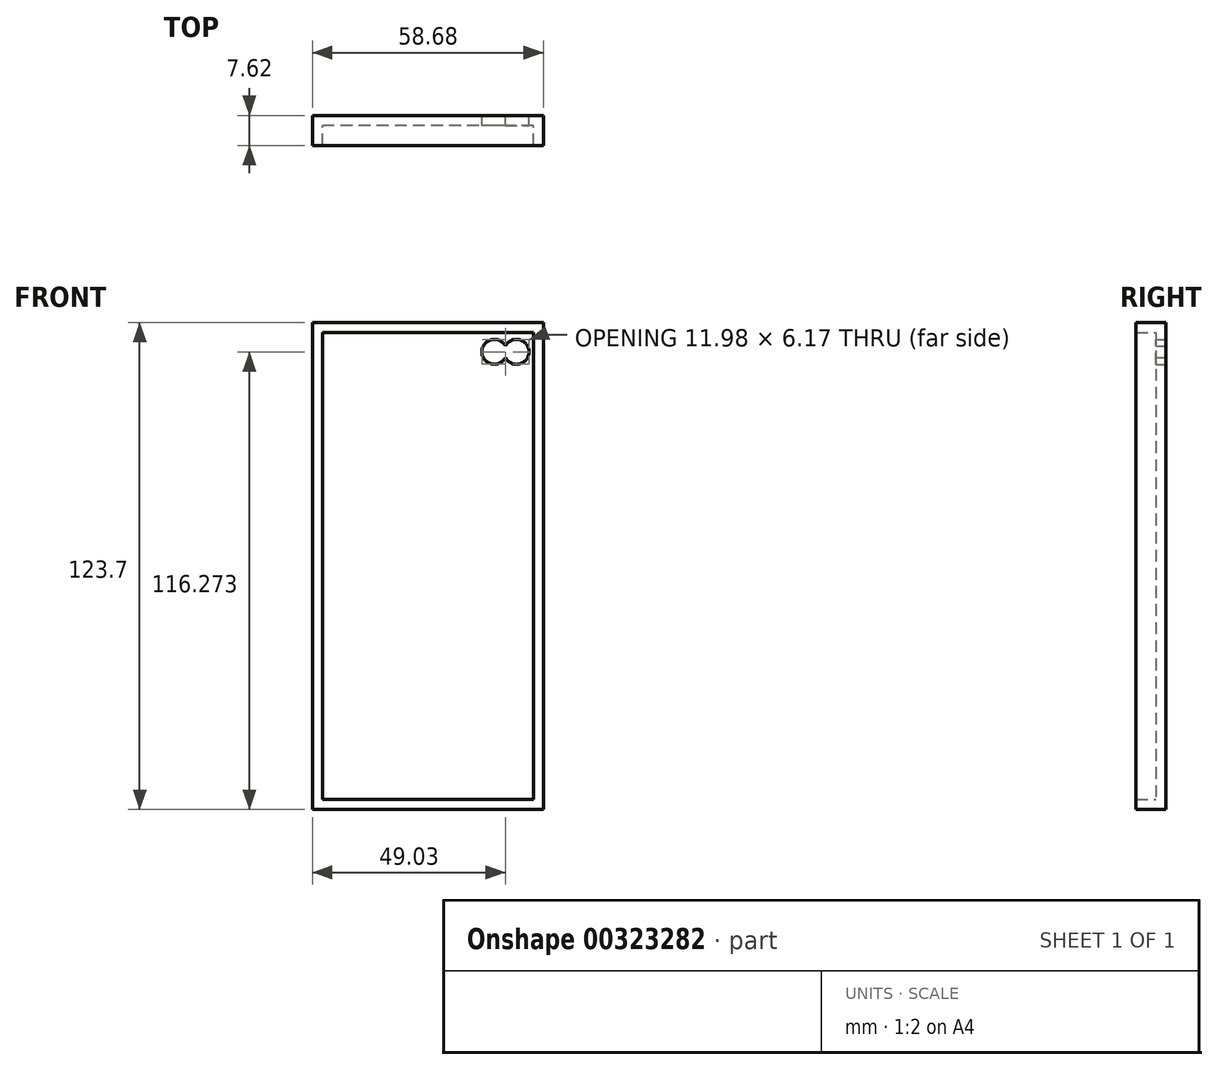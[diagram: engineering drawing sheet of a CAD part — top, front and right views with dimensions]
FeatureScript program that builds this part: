
annotation { "Feature Type Name" : "Feature", "Feature Type Description" : "" }
export const myFeature = defineFeature(function(context is Context, id is Id, definition is map)
    precondition{}
    {
        {
            var Q0;
            Q0=qCreatedBy(makeId("Front.planeOp"),FACE);
            var sketch = newSketch(context, id + "F0", { "sketchPlane" : qUnion([Q0])});
            skLineSegment(sketch, "E0", {"start": v(-16.17, 61.58) * mm, "end": v(-16.17, -62.12) * mm});
            skLineSegment(sketch, "E1", {"start": v(-16.17, -62.12) * mm, "end": v(42.5, -62.12) * mm});
            skLineSegment(sketch, "E2", {"start": v(42.5, -62.12) * mm, "end": v(42.5, 61.58) * mm});
            skLineSegment(sketch, "E3", {"start": v(42.5, 61.58) * mm, "end": v(-16.17, 61.58) * mm});
            skSolve(sketch);
        }
        {
            var Q0;
            Q0 = qSketchRegion(id + "F0", true);
            extrude(context, id + "F1", {"entities" : qUnion([Q0]), "depth" : 7.62 * mm});
        }
        {
            var Q0;
            Q0=makeQuery(id+"F1.opExtrude","CAP_FACE",FACE,{"disambiguationData":[OSD([sQuery(id+"F0.wireOp",EDGE,"E0"),sQuery(id+"F0.wireOp",EDGE,"E1"),sQuery(id+"F0.wireOp",EDGE,"E2"),sQuery(id+"F0.wireOp",EDGE,"E3")])],"isStart":false});
            shell(context, id + "F2", {"entities" : qUnion([Q0]), "thickness" : 2.54 * mm});
        }
        {
            var Q0;
            Q0=qCreatedBy(makeId("Front.planeOp"),FACE);
            var sketch = newSketch(context, id + "F3", { "sketchPlane" : qUnion([Q0])});
            skPoint(sketch, "E4", {"position": v(30.04, 54.15) * mm});
            skPoint(sketch, "E5", {"position": v(35.68, 54.15) * mm});
            skSolve(sketch);
        }
        {
            var Q0;
            Q0=sQuery(id+"F3.wireOp",VERTEX,"E4");
            var Q1;
            Q1=sQuery(id+"F3.wireOp",VERTEX,"E5");
            var Q2;
            Q2=makeQuery(id+"F1.opExtrude","SWEPT_BODY",BODY,{"disambiguationData":[OSD([sQuery(id+"F0.wireOp",EDGE,"E0"),sQuery(id+"F0.wireOp",EDGE,"E1"),sQuery(id+"F0.wireOp",EDGE,"E2"),sQuery(id+"F0.wireOp",EDGE,"E3")])]});
            hole(context, id + "F4", {"style" : HoleStyle.SIMPLE, "endStyle" : HoleEndStyle.THROUGH, "oppositeDirection" : true, "holeDiameter" : 6.35 * mm, "tappedDepth" : 12.7 * mm, "tapClearance" : 3, "locations" : qUnion([Q0, Q1]), "scope" : qUnion([Q2])});
        }
    });
